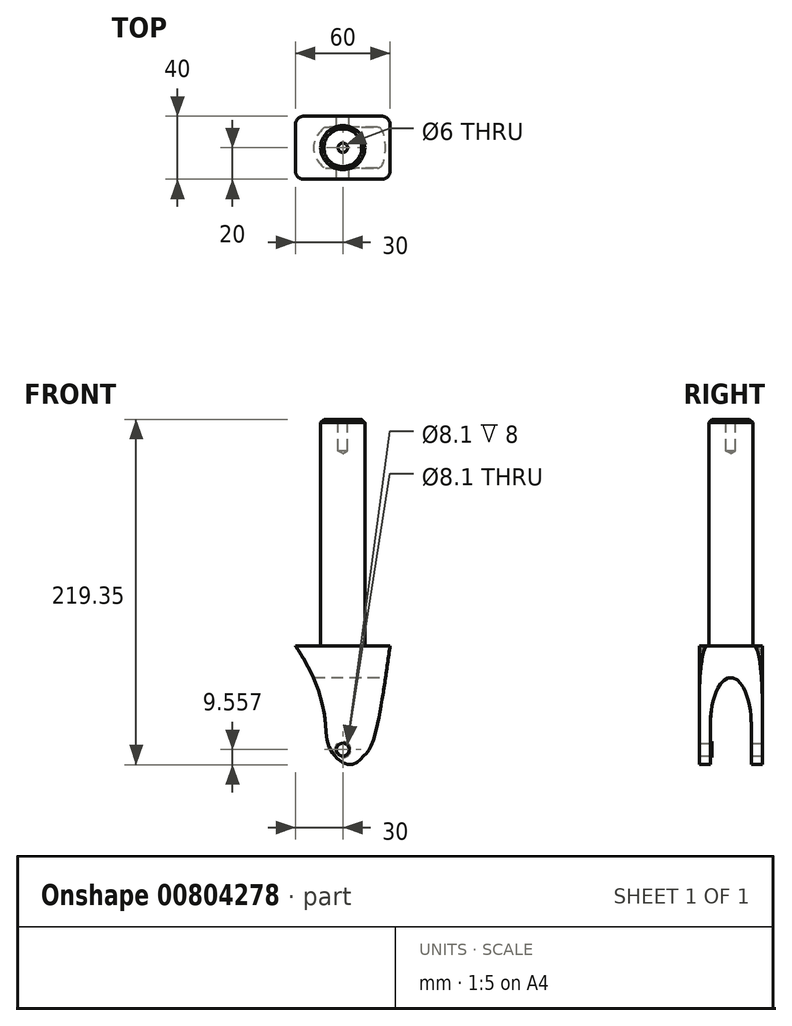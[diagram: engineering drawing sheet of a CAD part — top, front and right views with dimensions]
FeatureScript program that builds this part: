
annotation { "Feature Type Name" : "Feature", "Feature Type Description" : "" }
export const myFeature = defineFeature(function(context is Context, id is Id, definition is map)
    precondition{}
    {
        {
            var Q0;
            Q0=qCreatedBy(makeId("Top.planeOp"),FACE);
            var sketch = newSketch(context, id + "F0", { "sketchPlane" : qUnion([Q0])});
            skCircle(sketch, "E0", {"center": v(0, 0) * mm, "radius": 14 * mm});
            skSolve(sketch);
        }
        {
            var Q0;
            Q0=makeQuery(id+"F0.imprint","IMPRINT",FACE,{"disambiguationData":[TD([[makeQuery(id+"F0.imprint","IMPRINT",EDGE,{"derivedFrom":sQuery(id+"F0.wireOp",EDGE,"E0")}),1.0]])]});
            extrude(context, id + "F1", {"entities" : qUnion([Q0]), "depth" : 144 * mm, "offsetDistance" : 25 * mm});
        }
        {
            var Q0;
            Q0=qCreatedBy(makeId("Top.planeOp"),FACE);
            var sketch = newSketch(context, id + "F2", { "sketchPlane" : qUnion([Q0])});
            skLineSegment(sketch, "E1.bottom", {"start": v(-30, 20) * mm, "end": v(30, 20) * mm});
            skLineSegment(sketch, "E1.top", {"start": v(-30, -20) * mm, "end": v(30, -20) * mm});
            skLineSegment(sketch, "E1.left", {"start": v(-30, 20) * mm, "end": v(-30, -20) * mm});
            skLineSegment(sketch, "E1.right", {"start": v(30, 20) * mm, "end": v(30, -20) * mm});
            skPoint(sketch, "E1.middle", {"position": v(0, 0) * mm});
            skSolve(sketch);
        }
        {
            var Q0;
            Q0=makeQuery(id+"F2.imprint","IMPRINT",FACE,{"disambiguationData":[TD([[makeQuery(id+"F2.imprint","IMPRINT",EDGE,{"derivedFrom":sQuery(id+"F2.wireOp",EDGE,"E1.bottom")}),-1.0]])]});
            extrude(context, id + "F3", {"entities" : qUnion([Q0]), "operationType" : NewBodyOperationType.ADD, "oppositeDirection" : true, "depth" : 80 * mm, "offsetDistance" : 25 * mm});
        }
        {
            var Q0;
            Q0=makeQuery(id+"F3.opExtrude","SWEPT_EDGE",EDGE,{"disambiguationData":[OSD([sQuery(id+"F2.wireOp",EDGE,"E1.top"),sQuery(id+"F2.wireOp",EDGE,"E1.left")])]});
            var Q1;
            Q1=makeQuery(id+"F3.opExtrude","SWEPT_EDGE",EDGE,{"disambiguationData":[OSD([sQuery(id+"F2.wireOp",EDGE,"E1.top"),sQuery(id+"F2.wireOp",EDGE,"E1.right")])]});
            var Q2;
            Q2=makeQuery(id+"F3.opExtrude","SWEPT_EDGE",EDGE,{"disambiguationData":[OSD([sQuery(id+"F2.wireOp",EDGE,"E1.bottom"),sQuery(id+"F2.wireOp",EDGE,"E1.left")])]});
            var Q3;
            Q3=makeQuery(id+"F3.opExtrude","SWEPT_EDGE",EDGE,{"disambiguationData":[OSD([sQuery(id+"F2.wireOp",EDGE,"E1.bottom"),sQuery(id+"F2.wireOp",EDGE,"E1.right")])]});
            fillet(context, id + "F4", {"entities" : qUnion([Q0, Q1, Q2, Q3]), "radius" : 5 * mm, "tangentPropagation" : true, "allowEdgeOverflow" : false});
        }
        {
            var Q0;
            Q0=qCreatedBy(makeId("Front.planeOp"),FACE);
            var sketch = newSketch(context, id + "F5", { "sketchPlane" : qUnion([Q0])});
            skLineSegment(sketch, "E2.bottom", {"start": v(-30, 0) * mm, "end": v(30, 0) * mm});
            skLineSegment(sketch, "E2.top", {"start": v(-30, -90) * mm, "end": v(30, -90) * mm});
            skLineSegment(sketch, "E2.left", {"start": v(-30, 0) * mm, "end": v(-30, -90) * mm});
            skLineSegment(sketch, "E2.right", {"start": v(30, 0) * mm, "end": v(30, -90) * mm});
            skFitSpline(sketch, "E3", {"points": [v(-30, 0) * mm, v(-8.35, -64.7) * mm, v(5, -75.34) * mm, v(13, -70.02) * mm, v(30, 0) * mm], "startDerivative": vector(214.1, -321.38) * mm, "endDerivative": vector(75.65, 551.16) * mm});
            skSolve(sketch);
        }
        {
            var Q0;
            Q0=makeQuery(id+"F5.imprint","IMPRINT",FACE,{"disambiguationData":[TD([[makeQuery(id+"F5.imprint","IMPRINT",EDGE,{"derivedFrom":sQuery(id+"F5.wireOp",EDGE,"E2.top")}),1.0]])]});
            extrude(context, id + "F6", {"entities" : qUnion([Q0]), "operationType" : NewBodyOperationType.REMOVE, "endBound" : BoundingType.SYMMETRIC, "oppositeDirection" : true, "depth" : 80 * mm, "offsetDistance" : 25 * mm});
        }
        {
            var Q0;
            Q0=qCreatedBy(makeId("Right.planeOp"),FACE);
            var sketch = newSketch(context, id + "F7", { "sketchPlane" : qUnion([Q0])});
            skEllipticalArc(sketch, "E4", {});
            skLineSegment(sketch, "E5", {"start": v(-13, -50) * mm, "end": v(-13, -80) * mm});
            skLineSegment(sketch, "E6", {"start": v(13, -50) * mm, "end": v(13, -80) * mm});
            skLineSegment(sketch, "E7", {"start": v(13, -80) * mm, "end": v(-13, -80) * mm});
            skEllipticalArc(sketch, "E8", {});
            const initialGuessF7  = {"E4": [0, -0.05, 0, 1, 0.03, 0.013, 4.71238898038469, 0], "E8": [0, -0.05, 0, 1, 0.03, 0.013, 0, 1.5707963267948966]};
            skSetInitialGuess(sketch, initialGuessF7);
            skSolve(sketch);
        }
        {
            var Q0;
            Q0=makeQuery(id+"F7.imprint","IMPRINT",FACE,{"disambiguationData":[TD([[makeQuery(id+"F7.imprint","IMPRINT",EDGE,{"derivedFrom":sQuery(id+"F7.wireOp",EDGE,"E4")}),1.0]])]});
            extrude(context, id + "F8", {"entities" : qUnion([Q0]), "operationType" : NewBodyOperationType.REMOVE, "endBound" : BoundingType.SYMMETRIC, "depth" : 70 * mm, "offsetDistance" : 25 * mm});
        }
        {
            var Q0;
            Q0=makeQuery(id+"F3.opExtrude","SWEPT_FACE",FACE,{"disambiguationData":[OSD([sQuery(id+"F2.wireOp",EDGE,"E1.bottom")])]});
            var sketch = newSketch(context, id + "F9", { "sketchPlane" : qUnion([Q0])});
            skPoint(sketch, "E9", {"position": v(0, -65.8) * mm});
            skSolve(sketch);
        }
        {
            var Q0;
            Q0=sQuery(id+"F9.wireOp",VERTEX,"E9");
            var Q1;
            Q1=makeQuery(id+"F1.opExtrude","SWEPT_BODY",BODY,{"disambiguationData":[OSD([sQuery(id+"F0.wireOp",EDGE,"E0")])]});
            hole(context, id + "F10", {"style" : HoleStyle.SIMPLE, "endStyle" : HoleEndStyle.THROUGH, "holeDiameter" : 8.1 * mm, "majorDiameter" : 5 * mm, "isTappedThrough" : true, "tappedDepth" : 12 * mm, "tapClearance" : 3, "locations" : qUnion([Q0]), "scope" : qUnion([Q1])});
        }
        {
            var Q0;
            Q0=makeQuery(id+"F8.boolean.opBoolean","COPY",FACE,{"derivedFrom":makeQuery(id+"F8.opExtrude","SWEPT_FACE",FACE,{"disambiguationData":[OSD([sQuery(id+"F7.wireOp",EDGE,"E5")])]})});
            var sketch = newSketch(context, id + "F11", { "sketchPlane" : qUnion([Q0])});
            skCircle(sketch, "E10.0", {"center": v(0, -65.8) * mm, "radius": 4.05 * mm});
            skCircle(sketch, "E11.0", {"center": v(0, -65.8) * mm, "radius": 5.05 * mm});
            skSolve(sketch);
        }
        {
            var Q0;
            Q0=makeQuery(id+"F11.imprint","IMPRINT",FACE,{"disambiguationData":[TD([[makeQuery(id+"F11.imprint","IMPRINT",EDGE,{"derivedFrom":sQuery(id+"F11.wireOp",EDGE,"E10.0")}),1.0]])]});
            extrude(context, id + "F12", {"entities" : qUnion([Q0]), "operationType" : NewBodyOperationType.ADD, "depth" : 1 * mm, "offsetDistance" : 25 * mm});
        }
        {
            var Q0;
            Q0=makeQuery(id+"F1.opExtrude","CAP_FACE",FACE,{"disambiguationData":[OSD([sQuery(id+"F0.wireOp",EDGE,"E0")])],"isStart":false});
            var sketch = newSketch(context, id + "F13", { "sketchPlane" : qUnion([Q0])});
            skPoint(sketch, "E12", {"position": v(0, 0) * mm});
            skSolve(sketch);
        }
        {
            var Q0;
            Q0=sQuery(id+"F13.wireOp",VERTEX,"E12");
            var Q1;
            Q1=makeQuery(id+"F1.opExtrude","SWEPT_BODY",BODY,{"disambiguationData":[OSD([sQuery(id+"F0.wireOp",EDGE,"E0")])]});
            hole(context, id + "F14", {"style" : HoleStyle.SIMPLE, "endStyle" : HoleEndStyle.BLIND, "holeDiameter" : 6 * mm, "majorDiameter" : 5 * mm, "holeDepth" : 20 * mm, "isTappedThrough" : true, "tappedDepth" : 12 * mm, "tapClearance" : 3, "locations" : qUnion([Q0]), "scope" : qUnion([Q1])});
        }
        {
            var Q0;
            Q0=makeQuery(id+"F1.opExtrude","CAP_EDGE",EDGE,{"disambiguationData":[OSD([sQuery(id+"F0.wireOp",EDGE,"E0")])],"isStart":false});
            chamfer(context, id + "F15", {"entities" : qUnion([Q0]), "width" : 2 * mm, "tangentPropagation" : true});
        }
    });
